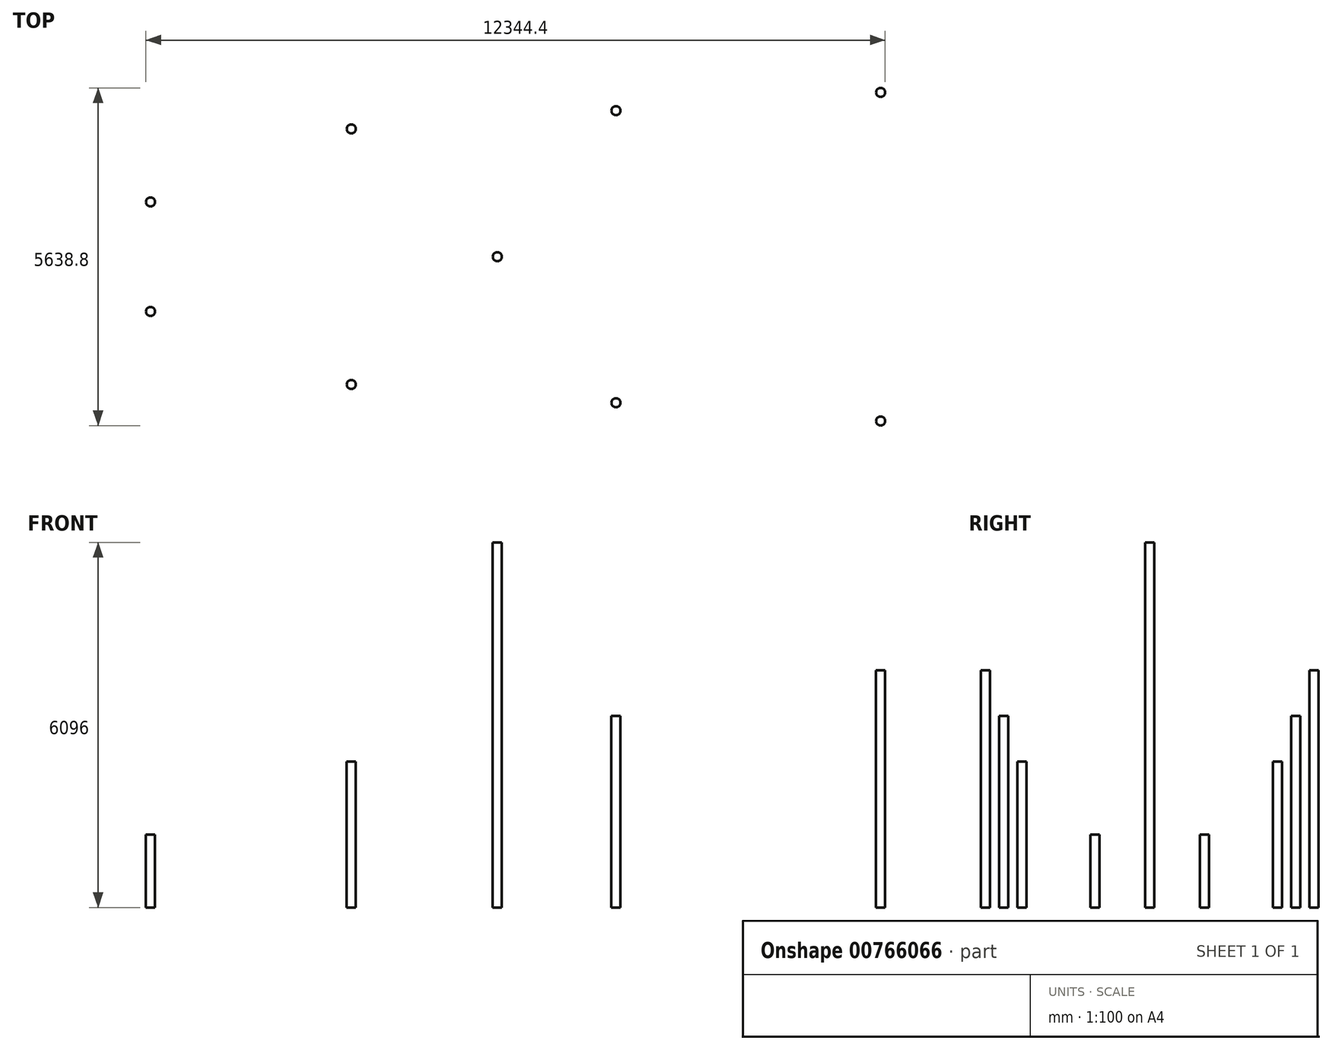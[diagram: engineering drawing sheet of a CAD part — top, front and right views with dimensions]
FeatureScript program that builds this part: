
annotation { "Feature Type Name" : "Feature", "Feature Type Description" : "" }
export const myFeature = defineFeature(function(context is Context, id is Id, definition is map)
    precondition{}
    {
        {
            var Q0;
            Q0=qCreatedBy(makeId("Top.planeOp"),FACE);
            var sketch = newSketch(context, id + "F0", { "sketchPlane" : qUnion([Q0])});
            skLineSegment(sketch, "E0", {"start": v(5638.8, 2743.2) * mm, "end": v(1219.2, 2438.4) * mm});
            skLineSegment(sketch, "E1", {"start": v(-3200.4, 2133.6) * mm, "end": v(-6553.2, 914.4) * mm});
            skLineSegment(sketch, "E2", {"start": v(-6553.2, 914.4) * mm, "end": v(-6553.2, -914.4) * mm});
            skLineSegment(sketch, "E3", {"start": v(-6553.2, -914.4) * mm, "end": v(-3200.4, -2133.6) * mm});
            skLineSegment(sketch, "E4", {"start": v(5638.8, -2743.2) * mm, "end": v(-762, 0) * mm});
            skLineSegment(sketch, "E5", {"start": v(-3200.4, 2133.6) * mm, "end": v(-762, 0) * mm});
            skLineSegment(sketch, "E6", {"start": v(5638.8, -2743.2) * mm, "end": v(1219.2, -2438.4) * mm});
            skLineSegment(sketch, "E7", {"start": v(-8077.2, -914.4) * mm, "end": v(-6553.2, -914.4) * mm});
            skLineSegment(sketch, "E8", {"start": v(-5638.8, -2743.2) * mm, "end": v(-6553.2, -914.4) * mm});
            skLineSegment(sketch, "E9", {"start": v(7772.4, -5181.6) * mm, "end": v(5638.8, -2743.2) * mm});
            skLineSegment(sketch, "E10", {"start": v(8077.2, -1524) * mm, "end": v(5638.8, -2743.2) * mm});
            skLineSegment(sketch, "E11", {"start": v(8077.2, 1524) * mm, "end": v(5638.8, 2743.2) * mm});
            skLineSegment(sketch, "E12", {"start": v(6858, 5181.6) * mm, "end": v(5638.8, 2743.2) * mm});
            skLineSegment(sketch, "E13", {"start": v(-8077.2, 914.4) * mm, "end": v(-6553.2, 914.4) * mm});
            skLineSegment(sketch, "E14", {"start": v(-5638.8, 3352.8) * mm, "end": v(-6553.2, 914.4) * mm});
            skLineSegment(sketch, "E15", {"start": v(5638.8, -2743.2) * mm, "end": v(5638.8, 2743.2) * mm});
            skLineSegment(sketch, "E16", {"start": v(1219.2, -2438.4) * mm, "end": v(-3200.4, -2133.6) * mm});
            skLineSegment(sketch, "E17", {"start": v(1219.2, -2438.4) * mm, "end": v(-304.8, -5181.6) * mm});
            skLineSegment(sketch, "E18", {"start": v(1219.2, -2438.4) * mm, "end": v(3048, -5181.6) * mm});
            skLineSegment(sketch, "E19", {"start": v(1219.2, 2438.4) * mm, "end": v(3048, 5181.6) * mm});
            skLineSegment(sketch, "E20", {"start": v(1219.2, 2438.4) * mm, "end": v(-304.8, 5181.6) * mm});
            skLineSegment(sketch, "E21", {"start": v(-762, 0) * mm, "end": v(-3200.4, -2133.6) * mm});
            skLineSegment(sketch, "E22", {"start": v(-762, 0) * mm, "end": v(5638.8, 2743.2) * mm});
            skLineSegment(sketch, "E23", {"start": v(1219.2, 2438.4) * mm, "end": v(-3200.4, 2133.6) * mm});
            skLineSegment(sketch, "E24", {"start": v(-3200.4, 2133.6) * mm, "end": v(-3200.4, -2133.6) * mm});
            skLineSegment(sketch, "E25", {"start": v(-3200.4, -2133.6) * mm, "end": v(-6553.2, 914.4) * mm});
            skLineSegment(sketch, "E26", {"start": v(-3200.4, 2133.6) * mm, "end": v(-6553.2, -914.4) * mm});
            skLineSegment(sketch, "E27", {"start": v(1219.2, -2438.4) * mm, "end": v(-762, 0) * mm});
            skLineSegment(sketch, "E28", {"start": v(-762, 0) * mm, "end": v(1219.2, 2438.4) * mm});
            skLineSegment(sketch, "E29", {"start": v(5638.8, -2743.2) * mm, "end": v(1219.2, 2438.4) * mm});
            skLineSegment(sketch, "E30", {"start": v(1219.2, -2438.4) * mm, "end": v(5638.8, 2743.2) * mm});
            skLineSegment(sketch, "E31", {"start": v(1219.2, 2438.4) * mm, "end": v(-762, 0) * mm});
            skLineSegment(sketch, "E32", {"start": v(-762, 0) * mm, "end": v(1219.2, -2438.4) * mm});
            skLineSegment(sketch, "E33", {"start": v(-3200.4, -2133.6) * mm, "end": v(-762, 0) * mm});
            skLineSegment(sketch, "E34", {"start": v(-762, 0) * mm, "end": v(-3200.4, 2133.6) * mm});
            skLineSegment(sketch, "E35", {"start": v(5638.8, 2743.2) * mm, "end": v(3962.4, 5181.6) * mm});
            skLineSegment(sketch, "E36", {"start": v(-1219.2, 5181.6) * mm, "end": v(-3200.4, 2133.6) * mm});
            skLineSegment(sketch, "E37", {"start": v(-3200.4, 2133.6) * mm, "end": v(-4572, 5181.6) * mm});
            skLineSegment(sketch, "E38", {"start": v(5638.8, -2743.2) * mm, "end": v(3962.4, -5181.6) * mm});
            skLineSegment(sketch, "E39", {"start": v(-1219.2, -5181.6) * mm, "end": v(-3200.4, -2133.6) * mm});
            skLineSegment(sketch, "E40", {"start": v(-3200.4, -2133.6) * mm, "end": v(-4572, -5181.6) * mm});
            skSolve(sketch);
        }
        {
            var Q0;
            Q0=qCreatedBy(makeId("Top.planeOp"),FACE);
            var sketch = newSketch(context, id + "F1", { "sketchPlane" : qUnion([Q0])});
            skPoint(sketch, "E41.0", {"position": v(-6553.2, 914.4) * mm});
            skPoint(sketch, "E42.0", {"position": v(-6553.2, -914.4) * mm});
            skPoint(sketch, "E43.0", {"position": v(-3200.4, -2133.6) * mm});
            skPoint(sketch, "E44.0", {"position": v(-3200.4, 2133.6) * mm});
            skPoint(sketch, "E45.0", {"position": v(-762, 0) * mm});
            skPoint(sketch, "E46.0", {"position": v(1219.2, 2438.4) * mm});
            skPoint(sketch, "E47.0", {"position": v(1219.2, -2438.4) * mm});
            skPoint(sketch, "E48.0", {"position": v(5638.8, -2743.2) * mm});
            skPoint(sketch, "E49.0", {"position": v(5638.8, 2743.2) * mm});
            skCircle(sketch, "E50", {"center": v(-6553.2, 914.4) * mm, "radius": 76.2 * mm});
            skCircle(sketch, "E51", {"center": v(-6553.2, -914.4) * mm, "radius": 76.2 * mm});
            skCircle(sketch, "E52", {"center": v(-3200.4, 2133.6) * mm, "radius": 76.2 * mm});
            skCircle(sketch, "E53", {"center": v(-3200.4, -2133.6) * mm, "radius": 76.2 * mm});
            skCircle(sketch, "E54", {"center": v(-762, 0) * mm, "radius": 76.2 * mm});
            skCircle(sketch, "E55", {"center": v(1219.2, 2438.4) * mm, "radius": 76.2 * mm});
            skCircle(sketch, "E56", {"center": v(1219.2, -2438.4) * mm, "radius": 76.2 * mm});
            skCircle(sketch, "E57", {"center": v(5638.8, -2743.2) * mm, "radius": 76.2 * mm});
            skCircle(sketch, "E58", {"center": v(5638.8, 2743.2) * mm, "radius": 76.2 * mm});
            skSolve(sketch);
        }
        {
            var Q0;
            Q0=makeQuery(id+"F1.imprint","IMPRINT",FACE,{"disambiguationData":[TD([[makeQuery(id+"F1.imprint","IMPRINT",EDGE,{"derivedFrom":sQuery(id+"F1.wireOp",EDGE,"E50")}),1.0]])]});
            var Q1;
            Q1=makeQuery(id+"F1.imprint","IMPRINT",FACE,{"disambiguationData":[TD([[makeQuery(id+"F1.imprint","IMPRINT",EDGE,{"derivedFrom":sQuery(id+"F1.wireOp",EDGE,"E51")}),1.0]])]});
            extrude(context, id + "F2", {"entities" : qUnion([Q0, Q1]), "depth" : 1219.2 * mm, "offsetDistance" : 25.4 * mm});
        }
        {
            var Q0;
            Q0=makeQuery(id+"F1.imprint","IMPRINT",FACE,{"disambiguationData":[TD([[makeQuery(id+"F1.imprint","IMPRINT",EDGE,{"derivedFrom":sQuery(id+"F1.wireOp",EDGE,"E52")}),1.0]])]});
            var Q1;
            Q1=makeQuery(id+"F1.imprint","IMPRINT",FACE,{"disambiguationData":[TD([[makeQuery(id+"F1.imprint","IMPRINT",EDGE,{"derivedFrom":sQuery(id+"F1.wireOp",EDGE,"E53")}),1.0]])]});
            extrude(context, id + "F3", {"entities" : qUnion([Q0, Q1]), "depth" : 2438.4 * mm, "offsetDistance" : 30.48 * mm});
        }
        {
            var Q0;
            Q0=makeQuery(id+"F1.imprint","IMPRINT",FACE,{"disambiguationData":[TD([[makeQuery(id+"F1.imprint","IMPRINT",EDGE,{"derivedFrom":sQuery(id+"F1.wireOp",EDGE,"E54")}),1.0]])]});
            extrude(context, id + "F4", {"entities" : qUnion([Q0]), "depth" : 6096 * mm, "offsetDistance" : 30.48 * mm});
        }
        {
            var Q0;
            Q0=makeQuery(id+"F1.imprint","IMPRINT",FACE,{"disambiguationData":[TD([[makeQuery(id+"F1.imprint","IMPRINT",EDGE,{"derivedFrom":sQuery(id+"F1.wireOp",EDGE,"E55")}),1.0]])]});
            var Q1;
            Q1=makeQuery(id+"F1.imprint","IMPRINT",FACE,{"disambiguationData":[TD([[makeQuery(id+"F1.imprint","IMPRINT",EDGE,{"derivedFrom":sQuery(id+"F1.wireOp",EDGE,"E56")}),1.0]])]});
            extrude(context, id + "F5", {"entities" : qUnion([Q0, Q1]), "depth" : 3200.4 * mm, "offsetDistance" : 30.48 * mm});
        }
        {
            var Q0;
            Q0=makeQuery(id+"F1.imprint","IMPRINT",FACE,{"disambiguationData":[TD([[makeQuery(id+"F1.imprint","IMPRINT",EDGE,{"derivedFrom":sQuery(id+"F1.wireOp",EDGE,"E58")}),1.0]])]});
            var Q1;
            Q1=makeQuery(id+"F1.imprint","IMPRINT",FACE,{"disambiguationData":[TD([[makeQuery(id+"F1.imprint","IMPRINT",EDGE,{"derivedFrom":sQuery(id+"F1.wireOp",EDGE,"E57")}),1.0]])]});
            extrude(context, id + "F6", {"entities" : qUnion([Q0, Q1]), "depth" : 3962.4 * mm, "offsetDistance" : 30.48 * mm});
        }
        {
            var Q0;
            Q0=makeQuery(id+"F2.opExtrude","CAP_FACE",FACE,{"disambiguationData":[OSD([sQuery(id+"F1.wireOp",EDGE,"E51")])],"isStart":false});
            cPlane(context, id + "F7", {"entities" : qUnion([Q0]), "cplaneType" : CPlaneType.OFFSET, "offset" : 0 * mm, "width" : 152.4 * mm, "height" : 152.4 * mm});
        }
        {
            var Q0;
            Q0=qCreatedBy(id+"F7.planeOp",FACE);
            var sketch = newSketch(context, id + "F8", { "sketchPlane" : qUnion([Q0])});
            skPoint(sketch, "E59.0", {"position": v(-6553.2, -914.4) * mm});
            skPoint(sketch, "E60.0", {"position": v(-6553.2, 914.4) * mm});
            skSolve(sketch);
        }
        {
            var Q0;
            Q0=makeQuery(id+"F3.opExtrude","CAP_FACE",FACE,{"disambiguationData":[OSD([sQuery(id+"F1.wireOp",EDGE,"E52")])],"isStart":false});
            cPlane(context, id + "F9", {"entities" : qUnion([Q0]), "cplaneType" : CPlaneType.OFFSET, "offset" : 0 * mm, "width" : 152.4 * mm, "height" : 152.4 * mm});
        }
        {
            var Q0;
            Q0=qCreatedBy(id+"F9.planeOp",FACE);
            var sketch = newSketch(context, id + "F10", { "sketchPlane" : qUnion([Q0])});
            skCircle(sketch, "E61.0.0", {"center": v(-3200.4, 2133.6) * mm, "radius": 76.2 * mm});
            skCircle(sketch, "E62.0.0", {"center": v(-762, 0) * mm, "radius": 76.2 * mm});
            skCircle(sketch, "E63.0.0", {"center": v(-3200.4, -2133.6) * mm, "radius": 76.2 * mm});
            skSolve(sketch);
        }
        {
            var Q0;
            Q0=makeQuery(id+"F4.opExtrude","CAP_FACE",FACE,{"disambiguationData":[OSD([sQuery(id+"F1.wireOp",EDGE,"E54")])],"isStart":false});
            cPlane(context, id + "F11", {"entities" : qUnion([Q0]), "cplaneType" : CPlaneType.OFFSET, "offset" : 0 * mm, "width" : 152.4 * mm, "height" : 152.4 * mm});
        }
        {
            var Q0;
            Q0=qCreatedBy(id+"F11.planeOp",FACE);
            var sketch = newSketch(context, id + "F12", { "sketchPlane" : qUnion([Q0])});
            skPoint(sketch, "E64.0", {"position": v(-762, 0) * mm});
            skSolve(sketch);
        }
        {
            var Q0;
            Q0=makeQuery(id+"F5.opExtrude","CAP_FACE",FACE,{"disambiguationData":[OSD([sQuery(id+"F1.wireOp",EDGE,"E55")])],"isStart":false});
            cPlane(context, id + "F13", {"entities" : qUnion([Q0]), "cplaneType" : CPlaneType.OFFSET, "offset" : 0 * mm, "width" : 152.4 * mm, "height" : 152.4 * mm});
        }
        {
            var Q0;
            Q0=qCreatedBy(id+"F13.planeOp",FACE);
            var sketch = newSketch(context, id + "F14", { "sketchPlane" : qUnion([Q0])});
            skCircle(sketch, "E65.0.0", {"center": v(1219.2, 2438.4) * mm, "radius": 76.2 * mm});
            skCircle(sketch, "E66.0.0", {"center": v(1219.2, -2438.4) * mm, "radius": 76.2 * mm});
            skSolve(sketch);
        }
        {
            var Q0;
            Q0=makeQuery(id+"F6.opExtrude","CAP_FACE",FACE,{"disambiguationData":[OSD([sQuery(id+"F1.wireOp",EDGE,"E57")])],"isStart":false});
            cPlane(context, id + "F15", {"entities" : qUnion([Q0]), "cplaneType" : CPlaneType.OFFSET, "offset" : 0 * mm, "width" : 152.4 * mm, "height" : 152.4 * mm});
        }
        {
            var Q0;
            Q0=qCreatedBy(id+"F15.planeOp",FACE);
            var sketch = newSketch(context, id + "F16", { "sketchPlane" : qUnion([Q0])});
            skCircle(sketch, "E67.0.0", {"center": v(5638.8, -2743.2) * mm, "radius": 76.2 * mm});
            skCircle(sketch, "E68.0", {"center": v(5638.8, 2743.2) * mm, "radius": 76.2 * mm});
            skSolve(sketch);
        }
        {
            var Q0;
            Q0=qCreatedBy(makeId("Top.planeOp"),FACE);
            var sketch = newSketch(context, id + "F17", { "sketchPlane" : qUnion([Q0])});
            skPoint(sketch, "E69.0", {"position": v(-8077.2, -914.4) * mm});
            skPoint(sketch, "E70.0", {"position": v(-5638.8, -2743.2) * mm});
            skPoint(sketch, "E71.0", {"position": v(-4572, -5181.6) * mm});
            skPoint(sketch, "E72.0", {"position": v(-1219.2, -5181.6) * mm});
            skPoint(sketch, "E73.0", {"position": v(-304.8, -5181.6) * mm});
            skPoint(sketch, "E74.0", {"position": v(3048, -5181.6) * mm});
            skPoint(sketch, "E75.0", {"position": v(3962.4, -5181.6) * mm});
            skPoint(sketch, "E76.0", {"position": v(7772.4, -5181.6) * mm});
            skPoint(sketch, "E77.0", {"position": v(8077.2, -1524) * mm});
            skPoint(sketch, "E78.0", {"position": v(8077.2, 1524) * mm});
            skPoint(sketch, "E79.0", {"position": v(6858, 5181.6) * mm});
            skPoint(sketch, "E80.0", {"position": v(3962.4, 5181.6) * mm});
            skPoint(sketch, "E81.0", {"position": v(3048, 5181.6) * mm});
            skPoint(sketch, "E82.0", {"position": v(-304.8, 5181.6) * mm});
            skPoint(sketch, "E83.0", {"position": v(-1219.2, 5181.6) * mm});
            skPoint(sketch, "E84.0", {"position": v(-4572, 5181.6) * mm});
            skPoint(sketch, "E85.0", {"position": v(-5638.8, 3352.8) * mm});
            skPoint(sketch, "E86.0", {"position": v(-8077.2, 914.4) * mm});
            skFitSpline(sketch, "E87", {"points": [v(-8077.2, -914.4) * mm, v(-5638.8, -2743.2) * mm, v(-4572, -5181.6) * mm, v(-1219.2, -5181.6) * mm, v(-304.8, -5181.6) * mm, v(3048, -5181.6) * mm, v(3962.4, -5181.6) * mm, v(7772.4, -5181.6) * mm, v(8077.2, -1524) * mm], "startDerivative": vector(6938.51, -18194.9) * mm, "endDerivative": vector(-6044.6, 33044.93) * mm});
            skFitSpline(sketch, "E88", {"points": [v(-8077.2, 914.4) * mm, v(-5638.8, 3352.8) * mm, v(-4572, 5181.6) * mm, v(-1219.2, 5181.6) * mm, v(-304.8, 5181.6) * mm, v(3048, 5181.6) * mm, v(3962.4, 5181.6) * mm, v(6858, 5181.6) * mm, v(8077.2, 1524) * mm], "startDerivative": vector(7818.36, 25727.94) * mm, "endDerivative": vector(2664.8, -30161) * mm});
            skSolve(sketch);
        }
        {
            var Q0;
            Q0=qCreatedBy(makeId("Right.planeOp"),FACE);
            var Q1;
            Q1=sQuery(id+"F16.wireOp",VERTEX,"E68.0.center");
            cPlane(context, id + "F18", {"entities" : qUnion([Q0, Q1]), "cplaneType" : CPlaneType.PLANE_POINT, "offset" : 25.4 * mm, "width" : 152.4 * mm, "height" : 152.4 * mm});
        }
        {
            var Q0;
            Q0=qCreatedBy(id+"F18.planeOp",FACE);
            var sketch = newSketch(context, id + "F19", { "sketchPlane" : qUnion([Q0])});
            skPoint(sketch, "E89.0", {"position": v(5181.6, 0) * mm});
            skPoint(sketch, "E90.0", {"position": v(2743.2, 3962.4) * mm});
            skPoint(sketch, "E91.0", {"position": v(-2743.2, 3962.4) * mm});
            skPoint(sketch, "E92.0", {"position": v(-5181.6, 0) * mm});
            skFitSpline(sketch, "E93", {"points": [v(-5181.6, 0) * mm, v(-2743.2, 3962.4) * mm, v(2743.2, 3962.4) * mm, v(5181.6, 0) * mm], "startDerivative": vector(6060.54, 9237.23) * mm, "endDerivative": vector(6060.54, -9237.23) * mm});
            skSolve(sketch);
        }
        {
            var Q0;
            Q0=qCreatedBy(makeId("Right.planeOp"),FACE);
            var Q1;
            Q1=sQuery(id+"F17.wireOp",VERTEX,"E77.0");
            cPlane(context, id + "F20", {"entities" : qUnion([Q0, Q1]), "cplaneType" : CPlaneType.PLANE_POINT, "offset" : 25.4 * mm, "width" : 152.4 * mm, "height" : 152.4 * mm});
        }
        {
            var Q0;
            Q0=qCreatedBy(id+"F20.planeOp",FACE);
            var sketch = newSketch(context, id + "F21", { "sketchPlane" : qUnion([Q0])});
            skPoint(sketch, "E94.0", {"position": v(-1524, 0) * mm});
            skPoint(sketch, "E95.0", {"position": v(1524, 0) * mm});
            skFitSpline(sketch, "E96", {"points": [v(-1524, 0) * mm, v(1524, 0) * mm], "startDerivative": vector(2758.74, 1489.39) * mm, "endDerivative": vector(2694.06, -1797.06) * mm});
            skSolve(sketch);
        }
        {
            var Q0;
            Q0=qCreatedBy(makeId("Right.planeOp"),FACE);
            var Q1;
            Q1=sQuery(id+"F14.wireOp",VERTEX,"E65.0.0.center");
            cPlane(context, id + "F22", {"entities" : qUnion([Q0, Q1]), "cplaneType" : CPlaneType.PLANE_POINT, "offset" : 25.4 * mm, "width" : 152.4 * mm, "height" : 152.4 * mm});
        }
        {
            var Q0;
            Q0=qCreatedBy(id+"F22.planeOp",FACE);
            var sketch = newSketch(context, id + "F23", { "sketchPlane" : qUnion([Q0])});
            skPoint(sketch, "E97.0", {"position": v(2438.4, 3200.4) * mm});
            skPoint(sketch, "E98.0", {"position": v(-2438.4, 3200.4) * mm});
            skPoint(sketch, "E99.0", {"position": v(-5181.6, 0) * mm});
            skPoint(sketch, "E100.0", {"position": v(5181.6, 0) * mm});
            skFitSpline(sketch, "E101", {"points": [v(-5181.6, 0) * mm, v(-2438.4, 3200.4) * mm, v(2438.4, 3200.4) * mm, v(5181.6, 0) * mm], "startDerivative": vector(6340.82, 13268.5) * mm, "endDerivative": vector(6340.82, -13268.5) * mm});
            skSolve(sketch);
        }
        {
            var Q0;
            Q0=sQuery(id+"F12.wireOp",VERTEX,"E64.0");
            var Q1;
            Q1=qCreatedBy(makeId("Right.planeOp"),FACE);
            cPlane(context, id + "F24", {"entities" : qUnion([Q0, Q1]), "cplaneType" : CPlaneType.PLANE_POINT, "offset" : 25.4 * mm, "width" : 152.4 * mm, "height" : 152.4 * mm});
        }
        {
            var Q0;
            Q0=qCreatedBy(id+"F24.planeOp",FACE);
            var sketch = newSketch(context, id + "F25", { "sketchPlane" : qUnion([Q0])});
            skPoint(sketch, "E102.0", {"position": v(0, 6096) * mm});
            skPoint(sketch, "E103.0", {"position": v(-5181.6, 0) * mm});
            skPoint(sketch, "E104.0", {"position": v(5181.6, 0) * mm});
            skFitSpline(sketch, "E105", {"points": [v(5181.6, 0) * mm, v(0, 6096) * mm, v(-5181.6, 0) * mm], "startDerivative": vector(-10081.02, 25468.23) * mm, "endDerivative": vector(-9352.96, -24838.71) * mm});
            skSolve(sketch);
        }
        {
            var Q0;
            Q0=sQuery(id+"F10.wireOp",VERTEX,"E61.0.0.center");
            var Q1;
            Q1=qCreatedBy(makeId("Right.planeOp"),FACE);
            cPlane(context, id + "F26", {"entities" : qUnion([Q0, Q1]), "cplaneType" : CPlaneType.PLANE_POINT, "offset" : 25.4 * mm, "width" : 152.4 * mm, "height" : 152.4 * mm});
        }
        {
            var Q0;
            Q0=qCreatedBy(id+"F26.planeOp",FACE);
            var sketch = newSketch(context, id + "F27", { "sketchPlane" : qUnion([Q0])});
            skPoint(sketch, "E106.0", {"position": v(2133.6, 2438.4) * mm});
            skPoint(sketch, "E107.0", {"position": v(5181.6, 0) * mm});
            skPoint(sketch, "E108.0", {"position": v(-5181.6, 0) * mm});
            skPoint(sketch, "E109.0", {"position": v(-2133.6, 2438.4) * mm});
            skFitSpline(sketch, "E110", {"points": [v(-5181.6, 0) * mm, v(-2133.6, 2438.4) * mm, v(2133.6, 2438.4) * mm, v(5181.6, 0) * mm], "startDerivative": vector(6987.73, 16009.76) * mm, "endDerivative": vector(6987.73, -16009.76) * mm});
            skSolve(sketch);
        }
        {
            var Q0;
            Q0=sQuery(id+"F8.wireOp",VERTEX,"E60.0");
            var Q1;
            Q1=qCreatedBy(makeId("Right.planeOp"),FACE);
            cPlane(context, id + "F28", {"entities" : qUnion([Q0, Q1]), "cplaneType" : CPlaneType.PLANE_POINT, "offset" : 25.4 * mm, "width" : 152.4 * mm, "height" : 152.4 * mm});
        }
        {
            var Q0;
            Q0=qCreatedBy(id+"F28.planeOp",FACE);
            var sketch = newSketch(context, id + "F29", { "sketchPlane" : qUnion([Q0])});
            skPoint(sketch, "E111.0", {"position": v(914.4, 1219.2) * mm});
            skPoint(sketch, "E112.0", {"position": v(-914.4, 1219.2) * mm});
            skPoint(sketch, "E113.0", {"position": v(3352.8, 0) * mm});
            skPoint(sketch, "E114.0", {"position": v(-2743.2, 0) * mm});
            skFitSpline(sketch, "E115", {"points": [v(3352.8, 0) * mm, v(914.4, 1219.2) * mm, v(-914.4, 1219.2) * mm, v(-2743.2, 0) * mm], "startDerivative": vector(-6750.27, 4019.07) * mm, "endDerivative": vector(-5421.23, -4502.47) * mm});
            skSolve(sketch);
        }
        {
            var Q0;
            Q0=qCreatedBy(makeId("Right.planeOp"),FACE);
            var Q1;
            Q1=sQuery(id+"F17.wireOp",VERTEX,"E86.0");
            cPlane(context, id + "F30", {"entities" : qUnion([Q0, Q1]), "cplaneType" : CPlaneType.PLANE_POINT, "offset" : 25.4 * mm, "width" : 152.4 * mm, "height" : 152.4 * mm});
        }
        {
            var Q0;
            Q0=qCreatedBy(id+"F30.planeOp",FACE);
            var sketch = newSketch(context, id + "F31", { "sketchPlane" : qUnion([Q0])});
            skPoint(sketch, "E116.0", {"position": v(914.4, 0) * mm});
            skPoint(sketch, "E117.0", {"position": v(-914.4, 0) * mm});
            skPoint(sketch, "E118.0", {"position": v(914.4, 1219.2) * mm});
            skPoint(sketch, "E119.0", {"position": v(-914.4, 1219.2) * mm});
            skFitSpline(sketch, "E120", {"points": [v(914.4, 0) * mm, v(914.4, 1219.2) * mm, v(-914.4, 1219.2) * mm, v(-914.4, 0) * mm], "startDerivative": vector(1493.2, 4624.5) * mm, "endDerivative": vector(1493.2, -4624.5) * mm});
            skSolve(sketch);
        }
        {
            var Q0;
            Q0=sQuery(id+"F31.wireOp",EDGE,"E120");
            var Q1;
            Q1=sQuery(id+"F29.wireOp",EDGE,"E115");
            var Q2;
            Q2=sQuery(id+"F27.wireOp",EDGE,"E110");
            var Q3;
            Q3=sQuery(id+"F25.wireOp",EDGE,"E105");
            var Q4;
            Q4=sQuery(id+"F23.wireOp",EDGE,"E101");
            var Q5;
            Q5=sQuery(id+"F19.wireOp",EDGE,"E93");
            var Q6;
            Q6=sQuery(id+"F21.wireOp",EDGE,"E96");
            loft(context, id + "F32", {"bodyType" : ToolBodyType.SURFACE, "wireProfilesArray" : [{ "wireProfileEntities" : qUnion([Q0]) }, { "wireProfileEntities" : qUnion([Q1]) }, { "wireProfileEntities" : qUnion([Q2]) }, { "wireProfileEntities" : qUnion([Q3]) }, { "wireProfileEntities" : qUnion([Q4]) }, { "wireProfileEntities" : qUnion([Q5]) }, { "wireProfileEntities" : qUnion([Q6]) }]});
        }
    });
